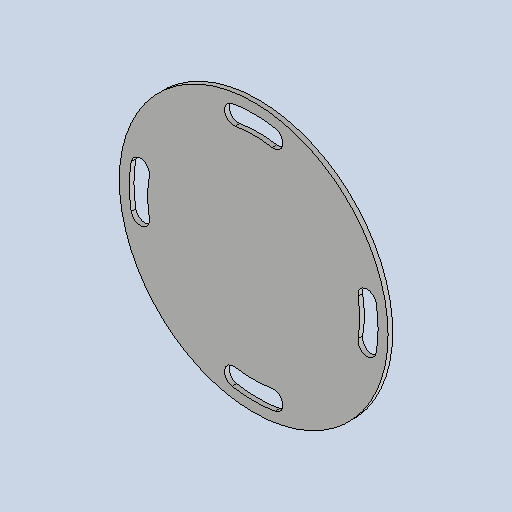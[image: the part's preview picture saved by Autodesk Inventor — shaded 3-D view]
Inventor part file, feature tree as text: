
AUTODESK INVENTOR PART (.ipt)
format: ipt  version: 2025 (Build 290162010, 162A)  size: 125,440 bytes
history: native  units: mm
features: sketch x2, sheet_metal_op x1, extrude x1, pattern_circular x1, other x1
ambient origin geometry x8: Origin, YZ Plane, XZ Plane, XY Plane, X Axis, Y Axis, Z Axis, Center Point
bodies: Solid1 (feature_tree)
feature tree (6):
  sheet_metal_op  "Face1"
  extrude  "Extrusion1"  Depth=3.0mm
  pattern_circular  "Circular Pattern1"  Count=4 Angle=360.0deg
  sketch  "Sketch1"  dims[d0=175.0mm d1=3.0mm]
  other  "Plate1"
  sketch  "Sketch2"  dims[d11=0.0mm d12=0.0mm d13=40.0mm d14=360.0deg d19=12.0mm d20=3.490659mm d21=75.0mm]
